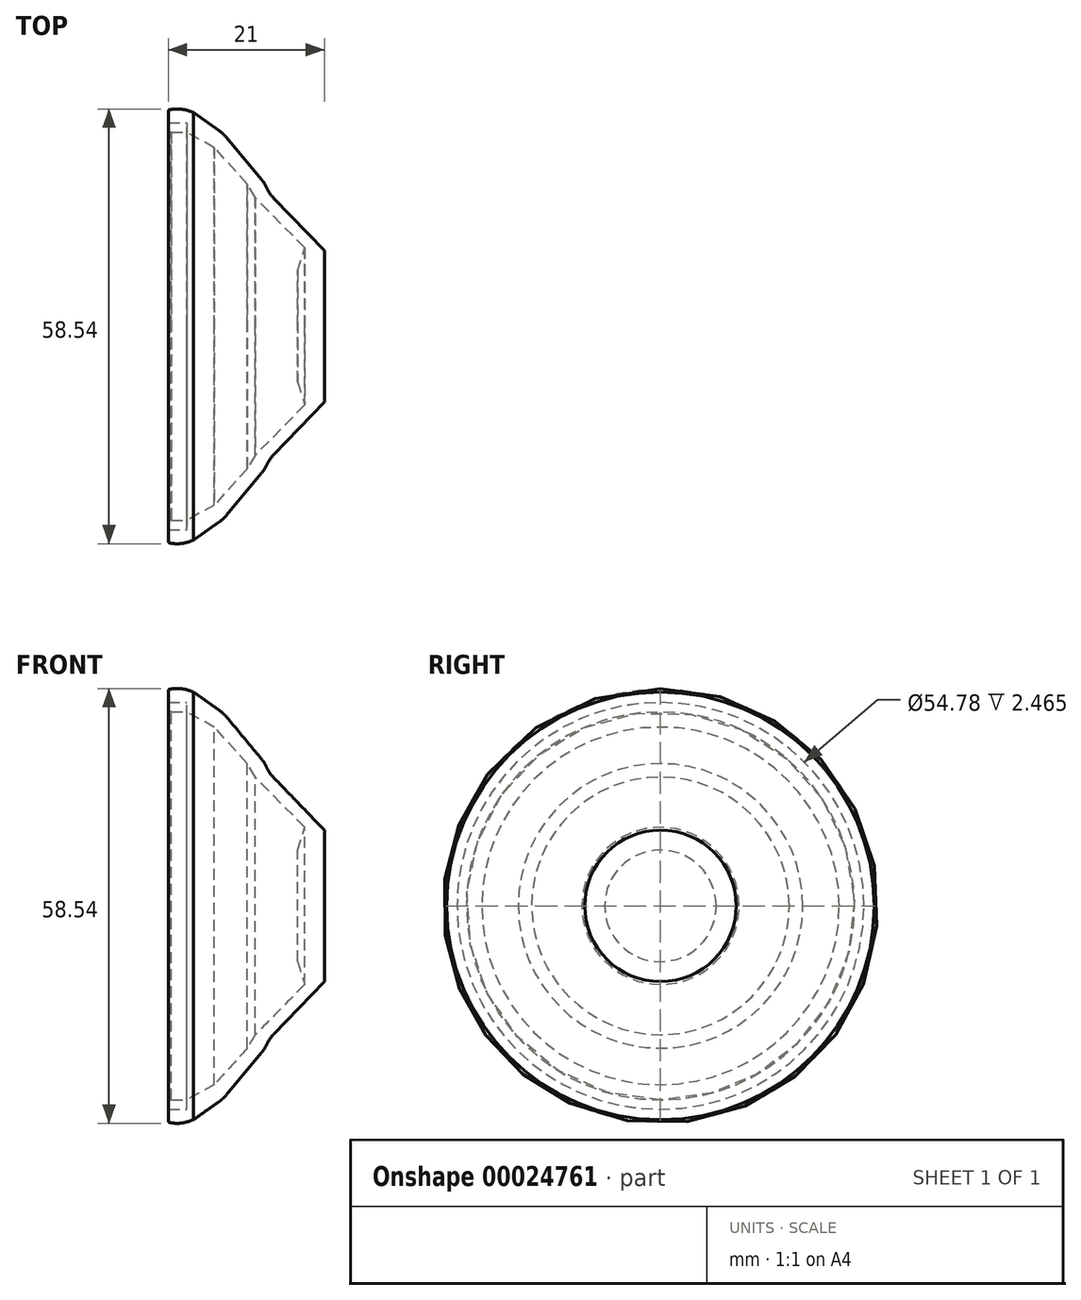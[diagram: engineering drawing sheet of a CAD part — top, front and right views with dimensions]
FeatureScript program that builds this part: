
annotation { "Feature Type Name" : "Feature", "Feature Type Description" : "" }
export const myFeature = defineFeature(function(context is Context, id is Id, definition is map)
    precondition{}
    {
        {
            var Q0;
            Q0=qCreatedBy(makeId("Front.planeOp"),FACE);
            var sketch = newSketch(context, id + "F0", { "sketchPlane" : qUnion([Q0])});
            skLineSegment(sketch, "E0", {"start": v(25.57, 0) * mm, "end": v(21.97, 0) * mm});
            skLineSegment(sketch, "E1", {"start": v(21.97, 0) * mm, "end": v(21.97, 7.51) * mm});
            skLineSegment(sketch, "E2", {"start": v(25.57, 0) * mm, "end": v(25.57, 10.2) * mm});
            skLineSegment(sketch, "E3", {"start": v(25.57, 10.2) * mm, "end": v(18.07, 17.99) * mm});
            skLineSegment(sketch, "E4", {"start": v(18.07, 17.99) * mm, "end": v(17.58, 19.21) * mm});
            skLineSegment(sketch, "E5", {"start": v(17.58, 19.21) * mm, "end": v(11.98, 25.94) * mm});
            skLineSegment(sketch, "E6", {"start": v(11.98, 25.94) * mm, "end": v(7.96, 28.79) * mm});
            skLineSegment(sketch, "E7", {"start": v(7.96, 28.79) * mm, "end": v(5.65, 29.67) * mm});
            skLineSegment(sketch, "E8", {"start": v(5.65, 29.67) * mm, "end": v(4.57, 29.13) * mm});
            skLineSegment(sketch, "E9", {"start": v(10.76, 24.08) * mm, "end": v(15.17, 19.17) * mm});
            skLineSegment(sketch, "E10", {"start": v(15.17, 19.17) * mm, "end": v(16.25, 17.35) * mm});
            skLineSegment(sketch, "E11", {"start": v(16.25, 17.35) * mm, "end": v(22.93, 10.57) * mm});
            skLineSegment(sketch, "E12", {"start": v(22.93, 10.57) * mm, "end": v(21.97, 7.51) * mm});
            skLineSegment(sketch, "E13", {"start": v(4.57, 29.13) * mm, "end": v(4.57, 27.4) * mm});
            skLineSegment(sketch, "E14", {"start": v(4.57, 27.4) * mm, "end": v(7.03, 27.4) * mm});
            skLineSegment(sketch, "E15", {"start": v(7.03, 27.4) * mm, "end": v(7.03, 26.11) * mm});
            skLineSegment(sketch, "E16", {"start": v(7.03, 26.11) * mm, "end": v(10.76, 24.08) * mm});
            skSolve(sketch);
        }
        {
            var Q0;
            Q0 = qSketchRegion(id + "F0", true);
            var Q1;
            Q1=sQuery(id+"F0.wireOp",EDGE,"E0");
            revolve(context, id + "F1", {"entities" : qUnion([Q0]), "axis" : qUnion([Q1]), "revolveType" : RevolveType.FULL});
        }
        {
            var Q0;
            Q0=makeQuery(id+"F1.opRevolve","SWEPT_EDGE",EDGE,{"disambiguationData":[OSD([sQuery(id+"F0.wireOp",EDGE,"E7"),sQuery(id+"F0.wireOp",EDGE,"E8")])]});
            fillet(context, id + "F2", {"entities" : qUnion([Q0]), "radius" : 5.08 * mm, "tangentPropagation" : true, "allowEdgeOverflow" : false});
        }
        {
            var Q0;
            Q0=makeQuery(id+"F1.opRevolve","SWEPT_EDGE",EDGE,{"disambiguationData":[OSD([sQuery(id+"F0.wireOp",EDGE,"E5"),sQuery(id+"F0.wireOp",EDGE,"E6")])]});
            fillet(context, id + "F3", {"entities" : qUnion([Q0]), "radius" : 5.08 * mm, "tangentPropagation" : true, "allowEdgeOverflow" : false});
        }
        {
            var Q0;
            Q0=makeQuery(id+"F1.opRevolve","SWEPT_EDGE",EDGE,{"disambiguationData":[OSD([sQuery(id+"F0.wireOp",EDGE,"E3"),sQuery(id+"F0.wireOp",EDGE,"E4")])]});
            fillet(context, id + "F4", {"entities" : qUnion([Q0]), "radius" : 5.08 * mm, "tangentPropagation" : true, "allowEdgeOverflow" : false});
        }
        {
            var Q0;
            Q0=makeQuery(id+"F1.opRevolve","SWEPT_EDGE",EDGE,{"disambiguationData":[OSD([sQuery(id+"F0.wireOp",EDGE,"E4"),sQuery(id+"F0.wireOp",EDGE,"E5")])]});
            fillet(context, id + "F5", {"entities" : qUnion([Q0]), "radius" : 5.08 * mm, "tangentPropagation" : true, "allowEdgeOverflow" : false});
        }
        {
            var Q0;
            Q0=qCreatedBy(makeId("Front.planeOp"),FACE);
            var sketch = newSketch(context, id + "F6", { "sketchPlane" : qUnion([Q0])});
            skLineSegment(sketch, "E17", {"start": v(4.58, 27.4) * mm, "end": v(7.03, 27.4) * mm});
            skLineSegment(sketch, "E18", {"start": v(7.03, 27.4) * mm, "end": v(7.03, 26.12) * mm});
            skLineSegment(sketch, "E19", {"start": v(4.58, 27.4) * mm, "end": v(4.58, 26.5) * mm});
            skLineSegment(sketch, "E20", {"start": v(7.03, 26.12) * mm, "end": v(5, 26.12) * mm});
            skArc(sketch, "E21", {"start": v(4.58, 26.5) * mm, "mid": v(4.7, 26.22) * mm, "end": v(5, 26.12) * mm});
            skSolve(sketch);
        }
        {
            var Q0;
            Q0 = qSketchRegion(id + "F6", true);
            var Q1;
            Q1=sQuery(id+"F0.wireOp",EDGE,"E0");
            revolve(context, id + "F7", {"entities" : qUnion([Q0]), "axis" : qUnion([Q1]), "revolveType" : RevolveType.FULL});
        }
    });
